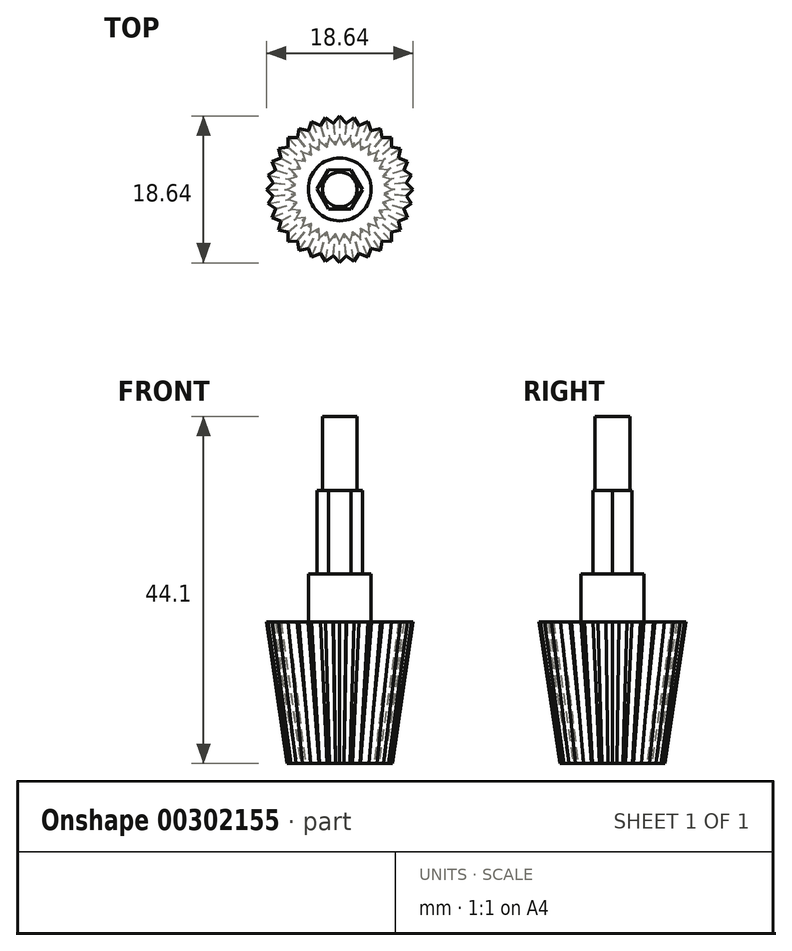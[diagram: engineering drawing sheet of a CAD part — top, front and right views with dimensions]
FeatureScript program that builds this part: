
annotation { "Feature Type Name" : "Feature", "Feature Type Description" : "" }
export const myFeature = defineFeature(function(context is Context, id is Id, definition is map)
    precondition{}
    {
        {
            var Q0;
            Q0=qCreatedBy(makeId("Top.planeOp"),FACE);
            var sketch = newSketch(context, id + "F0", { "sketchPlane" : qUnion([Q0])});
            skCircle(sketch, "E0", {"center": v(0, 0) * mm, "radius": 8.5 * mm});
            skSolve(sketch);
        }
        {
            var Q0;
            Q0=makeQuery(id+"F0.imprint","IMPRINT",FACE,{"disambiguationData":[TD([[makeQuery(id+"F0.imprint","IMPRINT",EDGE,{"derivedFrom":sQuery(id+"F0.wireOp",EDGE,"E0")}),1.0]])]});
            extrude(context, id + "F1", {"entities" : qUnion([Q0]), "oppositeDirection" : true, "depth" : 18 * mm, "hasDraft" : true, "draftAngle" : 9 * degree, "draftPullDirection" : true});
        }
        {
            var Q0;
            Q0=makeQuery(id+"F1.opExtrude","CAP_FACE",FACE,{"disambiguationData":[OSD([sQuery(id+"F0.wireOp",EDGE,"E0")])],"isStart":true});
            var sketch = newSketch(context, id + "F2", { "sketchPlane" : qUnion([Q0])});
            skCircle(sketch, "E1", {"center": v(0, 0) * mm, "radius": 4 * mm});
            skSolve(sketch);
        }
        {
            var Q0;
            Q0 = qSketchRegion(id + "F2", true);
            extrude(context, id + "F3", {"entities" : qUnion([Q0]), "operationType" : NewBodyOperationType.ADD, "depth" : 6.1 * mm});
        }
        {
            var Q0;
            Q0=makeQuery(id+"F3.opExtrude","CAP_FACE",FACE,{"disambiguationData":[OSD([sQuery(id+"F2.wireOp",EDGE,"E1")])],"isStart":false});
            var sketch = newSketch(context, id + "F4", { "sketchPlane" : qUnion([Q0])});
            skCircle(sketch, "E2.cCircle", {"center": v(0, 0) * mm, "radius": 2.49 * mm, "construction": true});
            skLineSegment(sketch, "E2.0", {"start": v(-2.87, 0.02) * mm, "end": v(-1.41, 2.5) * mm});
            skLineSegment(sketch, "E2.1", {"start": v(-1.41, 2.5) * mm, "end": v(1.46, 2.47) * mm});
            skLineSegment(sketch, "E2.2", {"start": v(1.46, 2.47) * mm, "end": v(2.87, -0.02) * mm});
            skLineSegment(sketch, "E2.3", {"start": v(2.87, -0.02) * mm, "end": v(1.41, -2.5) * mm});
            skLineSegment(sketch, "E2.4", {"start": v(1.41, -2.5) * mm, "end": v(-1.46, -2.47) * mm});
            skLineSegment(sketch, "E2.5", {"start": v(-1.46, -2.47) * mm, "end": v(-2.87, 0.02) * mm});
            skPoint(sketch, "E2.0.midPoint", {"position": v(-2.14, 1.26) * mm});
            skSolve(sketch);
        }
        {
            var Q0;
            Q0 = qSketchRegion(id + "F4", true);
            extrude(context, id + "F5", {"entities" : qUnion([Q0]), "operationType" : NewBodyOperationType.ADD, "depth" : 10.6 * mm});
        }
        {
            var Q0;
            Q0=makeQuery(id+"F5.opExtrude","CAP_FACE",FACE,{"disambiguationData":[OSD([sQuery(id+"F4.wireOp",EDGE,"E2.0"),sQuery(id+"F4.wireOp",EDGE,"E2.1"),sQuery(id+"F4.wireOp",EDGE,"E2.2"),sQuery(id+"F4.wireOp",EDGE,"E2.3"),sQuery(id+"F4.wireOp",EDGE,"E2.4"),sQuery(id+"F4.wireOp",EDGE,"E2.5")])],"isStart":false});
            var sketch = newSketch(context, id + "F6", { "sketchPlane" : qUnion([Q0])});
            skCircle(sketch, "E3", {"center": v(0, 0) * mm, "radius": 2.2 * mm});
            skSolve(sketch);
        }
        {
            var Q0;
            Q0 = qSketchRegion(id + "F6", true);
            extrude(context, id + "F7", {"entities" : qUnion([Q0]), "operationType" : NewBodyOperationType.ADD, "depth" : 9.4 * mm});
        }
        {
            var Q0;
            Q0=qCreatedBy(makeId("Top.planeOp"),FACE);
            var sketch = newSketch(context, id + "F8", { "sketchPlane" : qUnion([Q0])});
            skLineSegment(sketch, "E4", {"start": v(0, -9.32) * mm, "end": v(-0.82, -8.46) * mm});
            skLineSegment(sketch, "E5", {"start": v(-0.83, -8.46) * mm, "end": v(0.82, -8.46) * mm});
            skLineSegment(sketch, "E6", {"start": v(0.82, -8.46) * mm, "end": v(0, -9.32) * mm});
            skSolve(sketch);
        }
        {
            var Q0;
            Q0=makeQuery(id+"F1.opExtrude","CAP_FACE",FACE,{"disambiguationData":[OSD([sQuery(id+"F0.wireOp",EDGE,"E0")])],"isStart":false});
            var sketch = newSketch(context, id + "F9", { "sketchPlane" : qUnion([Q0])});
            skLineSegment(sketch, "E7.1.0", {"start": v(0, 6.68) * mm, "end": v(-0.55, 5.62) * mm});
            skLineSegment(sketch, "E7.1.1", {"start": v(0.55, 5.62) * mm, "end": v(0, 6.68) * mm});
            skLineSegment(sketch, "E7.1.2", {"start": v(-0.55, 5.62) * mm, "end": v(0.55, 5.62) * mm});
            skPoint(sketch, "E7.center", {"position": v(0, 0) * mm});
            skSolve(sketch);
        }
        {
            var Q0;
            Q0=qCreatedBy(makeId("Right.planeOp"),FACE);
            var sketch = newSketch(context, id + "F10", { "sketchPlane" : qUnion([Q0])});
            skLineSegment(sketch, "E8", {"start": v(0, 3.5) * mm, "end": v(0, -23.04) * mm, "construction": true});
            skSolve(sketch);
        }
        {
            var Q1;
            Q1=makeQuery(id+"F8.imprint","IMPRINT",FACE,{"disambiguationData":[TD([[makeQuery(id+"F8.imprint","IMPRINT",EDGE,{"derivedFrom":sQuery(id+"F8.wireOp",EDGE,"E4")}),-1.0]])]});
            var Q2;
            {var subQ0=sQuery(id+"F9.wireOp",EDGE,"E7.1.0");Q2=makeQuery(id+"F9.imprint","IMPRINT",FACE,{"disambiguationData":[TD([[makeQuery(id+"F9.imprint","IMPRINT",EDGE,{"derivedFrom":subQ0}),1.0]])]});}
            loft(context, id + "F11", {"sheetProfilesArray" : [{ "sheetProfileEntities" : qUnion([Q1]) }, { "sheetProfileEntities" : qUnion([Q2]) }]});
        }
        {
            var Q0;
            {var subQ0=sQuery(id+"F9.wireOp",EDGE,"E7.1.0");Q0=makeQuery(id+"F11.opLoft","SWEPT_BODY",BODY,{"disambiguationData":[OSD([makeQuery(id+"F8.imprint","IMPRINT",FACE,{"disambiguationData":[TD([[makeQuery(id+"F8.imprint","IMPRINT",EDGE,{"derivedFrom":sQuery(id+"F8.wireOp",EDGE,"E4")}),-1.0]])]}),makeQuery(id+"F9.imprint","IMPRINT",FACE,{"disambiguationData":[TD([[makeQuery(id+"F9.imprint","IMPRINT",EDGE,{"derivedFrom":subQ0}),1.0]])]})])]});}
            var Q1;
            Q1=sQuery(id+"F10.wireOp",EDGE,"E8");
            circularPattern(context, id + "F12", {"operationType" : NewBodyOperationType.ADD, "entities" : qUnion([Q0]), "axis" : qUnion([Q1]), "angle" : 360 * degree, "instanceCount" : 32, "equalSpace" : true});
        }
    });
